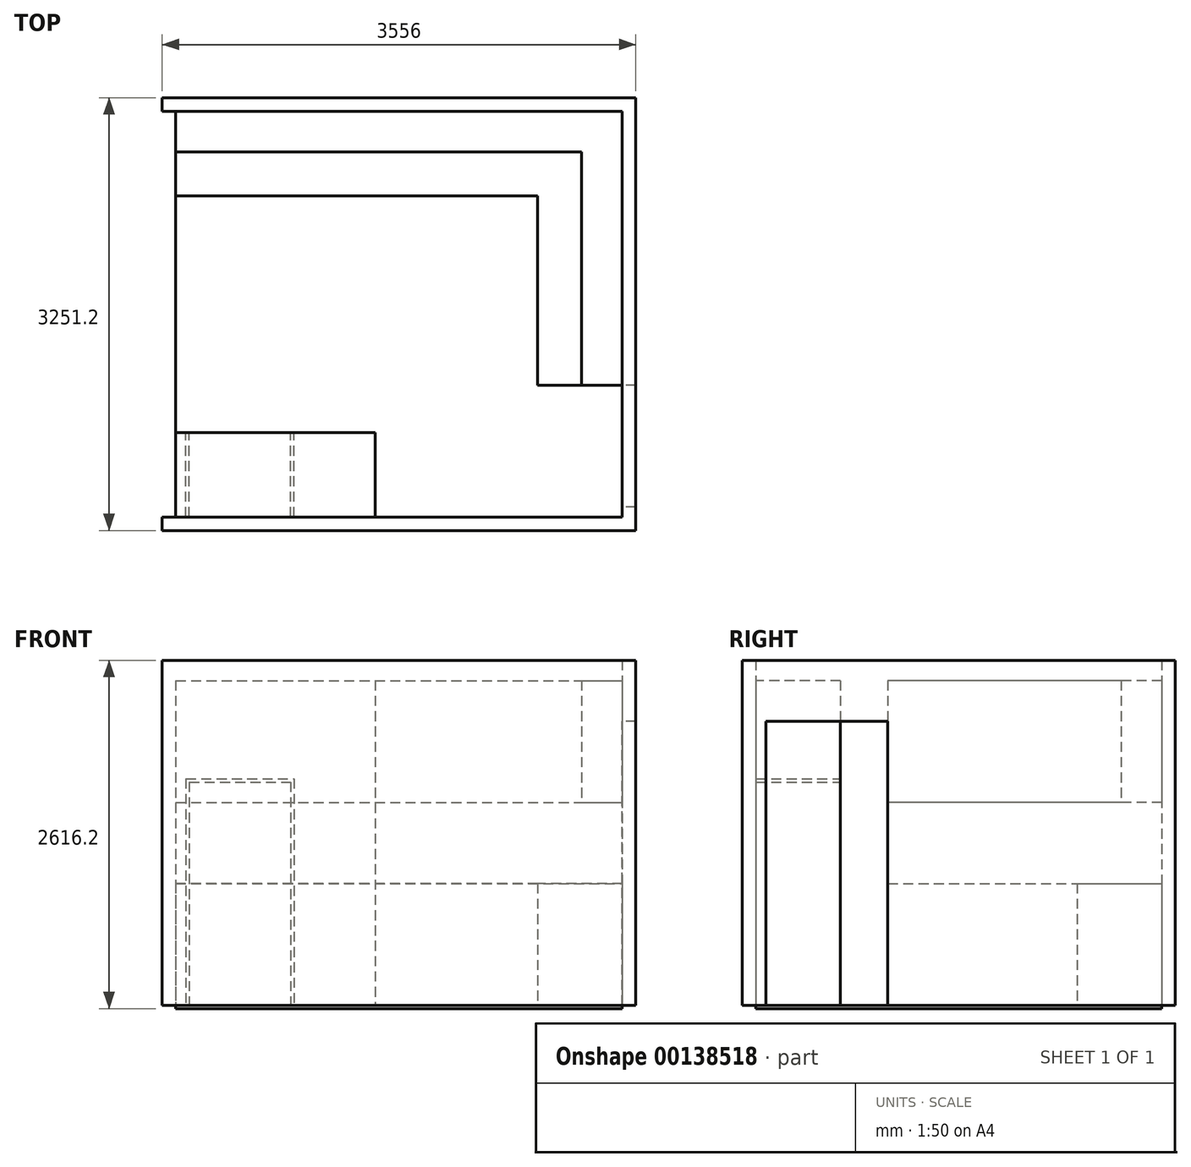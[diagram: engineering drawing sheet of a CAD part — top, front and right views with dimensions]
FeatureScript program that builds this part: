
annotation { "Feature Type Name" : "Feature", "Feature Type Description" : "" }
export const myFeature = defineFeature(function(context is Context, id is Id, definition is map)
    precondition{}
    {
        {
            var Q0;
            Q0=qCreatedBy(makeId("Top.planeOp"),FACE);
            var sketch = newSketch(context, id + "F0", { "sketchPlane" : qUnion([Q0])});
            skLineSegment(sketch, "E0.bottom", {"start": v(-1676.4, -1524) * mm, "end": v(1676.4, -1524) * mm});
            skLineSegment(sketch, "E0.top", {"start": v(-1676.4, 1524) * mm, "end": v(1676.4, 1524) * mm});
            skLineSegment(sketch, "E0.left", {"start": v(-1676.4, -1524) * mm, "end": v(-1676.4, 1524) * mm});
            skLineSegment(sketch, "E0.right", {"start": v(1676.4, -1524) * mm, "end": v(1676.4, 1524) * mm});
            skLineSegment(sketch, "E1", {"start": v(-1676.4, 1524) * mm, "end": v(1676.4, -1524) * mm, "construction": true});
            skLineSegment(sketch, "E2", {"start": v(-1676.4, -1524) * mm, "end": v(1676.4, 1524) * mm, "construction": true});
            skSolve(sketch);
        }
        {
            var Q0;
            Q0=makeQuery(id+"F0.imprint","IMPRINT",FACE,{"disambiguationData":[TD([[makeQuery(id+"F0.imprint","IMPRINT",EDGE,{"derivedFrom":sQuery(id+"F0.wireOp",EDGE,"E0.bottom")}),1.0]])]});
            extrude(context, id + "F1", {"entities" : qUnion([Q0]), "depth" : 25.4 * mm});
        }
        {
            var Q0;
            Q0=makeQuery(id+"F1.opExtrude","CAP_FACE",FACE,{"disambiguationData":[OSD([sQuery(id+"F0.wireOp",EDGE,"E0.bottom"),sQuery(id+"F0.wireOp",EDGE,"E0.top"),sQuery(id+"F0.wireOp",EDGE,"E0.left"),sQuery(id+"F0.wireOp",EDGE,"E0.right")])],"isStart":false});
            var sketch = newSketch(context, id + "F2", { "sketchPlane" : qUnion([Q0])});
            skLineSegment(sketch, "E3.1", {"start": v(-1676.4, 1524) * mm, "end": v(1676.4, 1524) * mm});
            skLineSegment(sketch, "E3.2", {"start": v(-1676.4, -1524) * mm, "end": v(-1676.4, 1524) * mm});
            skLineSegment(sketch, "E3.3", {"start": v(-1676.4, -1524) * mm, "end": v(1676.4, -1524) * mm});
            skLineSegment(sketch, "E3.4", {"start": v(1676.4, -1524) * mm, "end": v(1676.4, 1524) * mm});
            skLineSegment(sketch, "E4.0", {"start": v(-1778, 1625.6) * mm, "end": v(1778, 1625.6) * mm});
            skLineSegment(sketch, "E4.1", {"start": v(-1778, -1625.6) * mm, "end": v(-1778, 1625.6) * mm});
            skLineSegment(sketch, "E4.2", {"start": v(-1778, -1625.6) * mm, "end": v(1778, -1625.6) * mm});
            skLineSegment(sketch, "E4.3", {"start": v(1778, -1625.6) * mm, "end": v(1778, 1625.6) * mm});
            skSolve(sketch);
        }
        {
            var Q0;
            Q0=makeQuery(id+"F2.imprint","IMPRINT",FACE,{"disambiguationData":[TD([[makeQuery(id+"F2.imprint","IMPRINT",EDGE,{"derivedFrom":sQuery(id+"F2.wireOp",EDGE,"E3.1")}),1.0]])]});
            extrude(context, id + "F3", {"entities" : qUnion([Q0]), "depth" : 2590.8 * mm});
        }
        {
            var Q0;
            Q0=makeQuery(id+"F3.opExtrude","SWEPT_FACE",FACE,{"disambiguationData":[OSD([sQuery(id+"F2.wireOp",EDGE,"E3.4")])]});
            var sketch = newSketch(context, id + "F4", { "sketchPlane" : qUnion([Q0])});
            skLineSegment(sketch, "E5.bottom", {"start": v(1524, 25.4) * mm, "end": v(533.4, 25.4) * mm});
            skLineSegment(sketch, "E5.top", {"start": v(1447.8, 2159) * mm, "end": v(533.4, 2159) * mm});
            skLineSegment(sketch, "E5.left", {"start": v(1447.8, 25.4) * mm, "end": v(1447.8, 2159) * mm});
            skLineSegment(sketch, "E5.right", {"start": v(533.4, 25.4) * mm, "end": v(533.4, 2159) * mm});
            skSolve(sketch);
        }
        {
            var Q0;
            {var subQ1=sQuery(id+"F4.wireOp",EDGE,"E5.bottom");var subQ4=sQuery(id+"F4.wireOp",EDGE,"E5.left");var subQ5=makeQuery(id+"F4.imprint","INTERSECT",VERTEX,{"derivedFrom":[subQ1,subQ4]});Q0=makeQuery(id+"F4.imprint","IMPRINT",FACE,{"disambiguationData":[TD([[makeQuery(id+"F4.imprint","IMPRINT",EDGE,{"disambiguationData":[TD([[subQ5,-1.0]])],"derivedFrom":subQ4}),1.0]])]});}
            var Q1;
            Q1=makeQuery(id+"F3.opExtrude","SWEPT_FACE",FACE,{"disambiguationData":[OSD([sQuery(id+"F2.wireOp",EDGE,"E4.3")])]});
            extrude(context, id + "F5", {"entities" : qUnion([Q0]), "operationType" : NewBodyOperationType.REMOVE, "endBound" : BoundingType.UP_TO_SURFACE, "oppositeDirection" : true, "endBoundEntityFace" : qUnion([Q1]), "depth" : 25.4 * mm});
        }
        {
            var Q0;
            Q0=makeQuery(id+"F3.opExtrude","SWEPT_FACE",FACE,{"disambiguationData":[OSD([sQuery(id+"F2.wireOp",EDGE,"E3.2")])]});
            var sketch = newSketch(context, id + "F6", { "sketchPlane" : qUnion([Q0])});
            skLineSegment(sketch, "E6.bottom", {"start": v(1524, 25.4) * mm, "end": v(-1524, 25.4) * mm});
            skLineSegment(sketch, "E6.top", {"start": v(1524, 2616.2) * mm, "end": v(-1524, 2616.2) * mm});
            skLineSegment(sketch, "E6.left", {"start": v(1524, 25.4) * mm, "end": v(1524, 2616.2) * mm});
            skLineSegment(sketch, "E6.right", {"start": v(-1524, 25.4) * mm, "end": v(-1524, 2616.2) * mm});
            skSolve(sketch);
        }
        {
            var Q0;
            Q0=makeQuery(id+"F6.imprint","IMPRINT",FACE,{"disambiguationData":[TD([[makeQuery(id+"F6.imprint","IMPRINT",EDGE,{"derivedFrom":sQuery(id+"F6.wireOp",EDGE,"E6.bottom")}),1.0]])]});
            var Q1;
            Q1=makeQuery(id+"F3.opExtrude","SWEPT_FACE",FACE,{"disambiguationData":[OSD([sQuery(id+"F2.wireOp",EDGE,"E4.1")])]});
            extrude(context, id + "F7", {"entities" : qUnion([Q0]), "operationType" : NewBodyOperationType.REMOVE, "endBound" : BoundingType.UP_TO_SURFACE, "oppositeDirection" : true, "endBoundEntityFace" : qUnion([Q1]), "depth" : 25.4 * mm});
        }
        {
            var Q0;
            Q0=makeQuery(id+"F1.opExtrude","CAP_FACE",FACE,{"disambiguationData":[OSD([sQuery(id+"F0.wireOp",EDGE,"E0.bottom"),sQuery(id+"F0.wireOp",EDGE,"E0.top"),sQuery(id+"F0.wireOp",EDGE,"E0.left"),sQuery(id+"F0.wireOp",EDGE,"E0.right")])],"isStart":false});
            var sketch = newSketch(context, id + "F8", { "sketchPlane" : qUnion([Q0])});
            skLineSegment(sketch, "E7.0", {"start": v(1676.4, -533.4) * mm, "end": v(1676.4, 1524) * mm});
            skLineSegment(sketch, "E7.1", {"start": v(-1676.4, 1524) * mm, "end": v(1676.4, 1524) * mm});
            skLineSegment(sketch, "E8", {"start": v(1676.4, -533.4) * mm, "end": v(1041.4, -533.4) * mm});
            skLineSegment(sketch, "E9", {"start": v(1041.4, -533.4) * mm, "end": v(1041.4, 889) * mm});
            skLineSegment(sketch, "E10", {"start": v(1041.4, 889) * mm, "end": v(-1676.4, 889) * mm});
            skLineSegment(sketch, "E11", {"start": v(-1676.4, 889) * mm, "end": v(-1676.4, 1524) * mm});
            skPoint(sketch, "E12.orphan", {"position": v(-1778, 1524) * mm});
            skSolve(sketch);
        }
        {
            var Q0;
            Q0=makeQuery(id+"F8.imprint","IMPRINT",FACE,{"disambiguationData":[TD([[makeQuery(id+"F8.imprint","IMPRINT",EDGE,{"derivedFrom":sQuery(id+"F8.wireOp",EDGE,"E7.0")}),1.0]])]});
            extrude(context, id + "F9", {"entities" : qUnion([Q0]), "depth" : 914.4 * mm});
        }
        {
            var Q0;
            Q0=makeQuery(id+"F9.opExtrude","CAP_FACE",FACE,{"disambiguationData":[OSD([sQuery(id+"F8.wireOp",EDGE,"E7.0"),sQuery(id+"F8.wireOp",EDGE,"E7.1"),sQuery(id+"F8.wireOp",EDGE,"E8"),sQuery(id+"F8.wireOp",EDGE,"E9"),sQuery(id+"F8.wireOp",EDGE,"E10"),sQuery(id+"F8.wireOp",EDGE,"E11")])],"isStart":false});
            cPlane(context, id + "F10", {"entities" : qUnion([Q0]), "cplaneType" : CPlaneType.OFFSET, "offset" : 609.6 * mm, "width" : 152.4 * mm, "height" : 152.4 * mm});
        }
        {
            var Q0;
            Q0=qCreatedBy(id+"F10.planeOp",FACE);
            var sketch = newSketch(context, id + "F11", { "sketchPlane" : qUnion([Q0])});
            skLineSegment(sketch, "E13.0", {"start": v(-1676.4, 1524) * mm, "end": v(1676.4, 1524) * mm});
            skLineSegment(sketch, "E14", {"start": v(-1676.4, 1524) * mm, "end": v(-1676.4, 1219.2) * mm});
            skLineSegment(sketch, "E15", {"start": v(-1676.4, 1219.2) * mm, "end": v(1371.6, 1219.2) * mm});
            skLineSegment(sketch, "E16", {"start": v(1371.6, 1219.2) * mm, "end": v(1371.6, -533.4) * mm});
            skLineSegment(sketch, "E17", {"start": v(1371.6, -533.4) * mm, "end": v(1676.4, -533.4) * mm});
            skLineSegment(sketch, "E18", {"start": v(1676.4, 1524) * mm, "end": v(1676.4, -533.4) * mm});
            skSolve(sketch);
        }
        {
            var Q0;
            Q0=makeQuery(id+"F11.imprint","IMPRINT",FACE,{"disambiguationData":[TD([[makeQuery(id+"F11.imprint","IMPRINT",EDGE,{"derivedFrom":sQuery(id+"F11.wireOp",EDGE,"E13.0")}),-1.0]])]});
            extrude(context, id + "F12", {"entities" : qUnion([Q0]), "depth" : 914.4 * mm});
        }
        {
            var Q0;
            Q0=makeQuery(id+"F1.opExtrude","CAP_FACE",FACE,{"disambiguationData":[OSD([sQuery(id+"F0.wireOp",EDGE,"E0.bottom"),sQuery(id+"F0.wireOp",EDGE,"E0.top"),sQuery(id+"F0.wireOp",EDGE,"E0.left"),sQuery(id+"F0.wireOp",EDGE,"E0.right")])],"isStart":false});
            var sketch = newSketch(context, id + "F13", { "sketchPlane" : qUnion([Q0])});
            skLineSegment(sketch, "E19.bottom", {"start": v(-1574.8, -1524) * mm, "end": v(-812.8, -1524) * mm});
            skLineSegment(sketch, "E19.top", {"start": v(-1574.8, -889) * mm, "end": v(-812.8, -889) * mm});
            skLineSegment(sketch, "E19.left", {"start": v(-1574.8, -1524) * mm, "end": v(-1574.8, -889) * mm});
            skLineSegment(sketch, "E19.right", {"start": v(-812.8, -1524) * mm, "end": v(-812.8, -889) * mm});
            skSolve(sketch);
        }
        {
            var Q0;
            Q0=makeQuery(id+"F13.imprint","IMPRINT",FACE,{"disambiguationData":[TD([[makeQuery(id+"F13.imprint","IMPRINT",EDGE,{"derivedFrom":sQuery(id+"F13.wireOp",EDGE,"E19.bottom")}),1.0]])]});
            extrude(context, id + "F14", {"entities" : qUnion([Q0]), "depth" : 1676.4 * mm});
        }
        {
            var Q0;
            Q0=makeQuery(id+"F1.opExtrude","CAP_FACE",FACE,{"disambiguationData":[OSD([sQuery(id+"F0.wireOp",EDGE,"E0.bottom"),sQuery(id+"F0.wireOp",EDGE,"E0.top"),sQuery(id+"F0.wireOp",EDGE,"E0.left"),sQuery(id+"F0.wireOp",EDGE,"E0.right")])],"isStart":false});
            var sketch = newSketch(context, id + "F15", { "sketchPlane" : qUnion([Q0])});
            skLineSegment(sketch, "E20.bottom", {"start": v(-1676.4, -1524) * mm, "end": v(-1600.2, -1524) * mm});
            skLineSegment(sketch, "E20.top", {"start": v(-1676.4, -889) * mm, "end": v(-1600.2, -889) * mm});
            skLineSegment(sketch, "E20.left", {"start": v(-1676.4, -1524) * mm, "end": v(-1676.4, -889) * mm});
            skLineSegment(sketch, "E20.right", {"start": v(-1600.2, -1524) * mm, "end": v(-1600.2, -889) * mm});
            skLineSegment(sketch, "E21.bottom", {"start": v(-787.4, -1524) * mm, "end": v(-177.8, -1524) * mm});
            skLineSegment(sketch, "E21.top", {"start": v(-787.4, -889) * mm, "end": v(-177.8, -889) * mm});
            skLineSegment(sketch, "E21.left", {"start": v(-787.4, -1524) * mm, "end": v(-787.4, -889) * mm});
            skLineSegment(sketch, "E21.right", {"start": v(-177.8, -1524) * mm, "end": v(-177.8, -889) * mm});
            skSolve(sketch);
        }
        {
            var Q0;
            Q0=makeQuery(id+"F15.imprint","IMPRINT",FACE,{"disambiguationData":[TD([[makeQuery(id+"F15.imprint","IMPRINT",EDGE,{"derivedFrom":sQuery(id+"F15.wireOp",EDGE,"E21.bottom")}),1.0]])]});
            var Q1;
            Q1=makeQuery(id+"F15.imprint","IMPRINT",FACE,{"disambiguationData":[TD([[makeQuery(id+"F15.imprint","IMPRINT",EDGE,{"derivedFrom":sQuery(id+"F15.wireOp",EDGE,"E20.bottom")}),1.0]])]});
            extrude(context, id + "F16", {"entities" : qUnion([Q0, Q1]), "depth" : 1701.8 * mm});
        }
        {
            var Q0;
            Q0=makeQuery(id+"F16.opExtrude","CAP_FACE",FACE,{"disambiguationData":[OSD([sQuery(id+"F15.wireOp",EDGE,"E21.bottom"),sQuery(id+"F15.wireOp",EDGE,"E21.top"),sQuery(id+"F15.wireOp",EDGE,"E21.left"),sQuery(id+"F15.wireOp",EDGE,"E21.right")])],"isStart":false});
            var sketch = newSketch(context, id + "F17", { "sketchPlane" : qUnion([Q0])});
            skLineSegment(sketch, "E22.bottom", {"start": v(-177.8, -889) * mm, "end": v(-1676.4, -889) * mm});
            skLineSegment(sketch, "E22.top", {"start": v(-177.8, -1524) * mm, "end": v(-1676.4, -1524) * mm});
            skLineSegment(sketch, "E22.left", {"start": v(-177.8, -889) * mm, "end": v(-177.8, -1524) * mm});
            skLineSegment(sketch, "E22.right", {"start": v(-1676.4, -889) * mm, "end": v(-1676.4, -1524) * mm});
            skSolve(sketch);
        }
        {
            var Q0;
            Q0 = qSketchRegion(id + "F17", true);
            var Q1;
            Q1=makeQuery(id+"F12.opExtrude","CAP_FACE",FACE,{"disambiguationData":[OSD([sQuery(id+"F11.wireOp",EDGE,"bcdea74c-0be9-4b13-a195-7bfbb5e1d8e7.0"),sQuery(id+"F11.wireOp",EDGE,"E13.0"),sQuery(id+"F11.wireOp",EDGE,"E14"),sQuery(id+"F11.wireOp",EDGE,"E15"),sQuery(id+"F11.wireOp",EDGE,"E16"),sQuery(id+"F11.wireOp",EDGE,"E17")])],"isStart":false});
            extrude(context, id + "F18", {"entities" : qUnion([Q0]), "operationType" : NewBodyOperationType.ADD, "endBound" : BoundingType.UP_TO_SURFACE, "endBoundEntityFace" : qUnion([Q1]), "depth" : 25.4 * mm});
        }
    });
